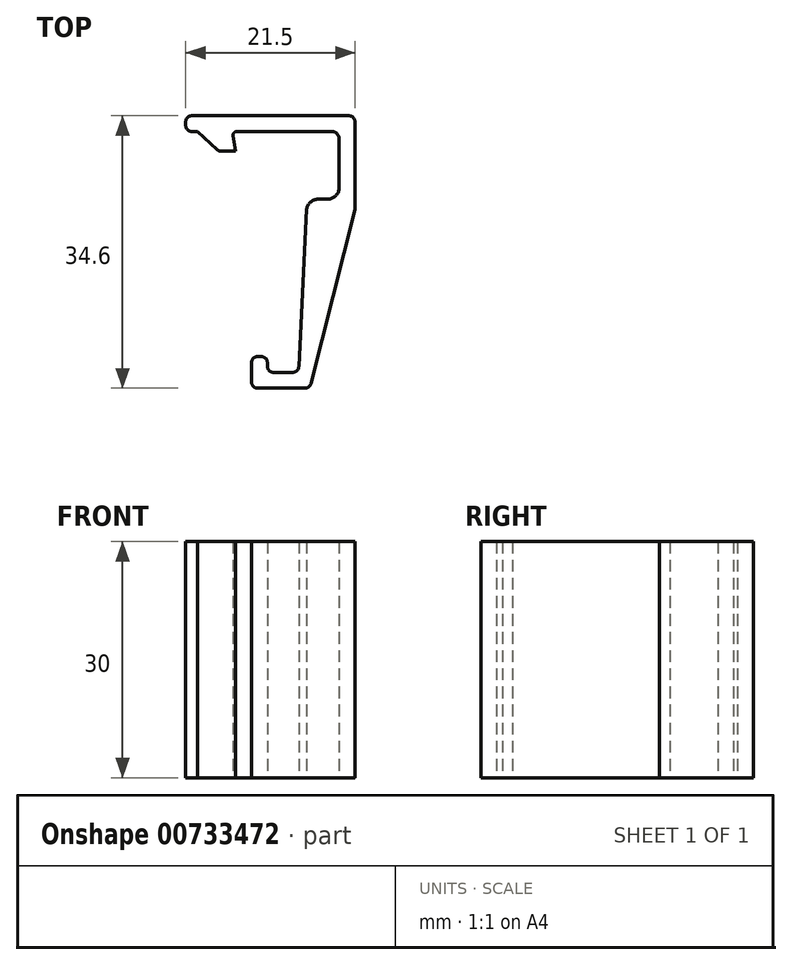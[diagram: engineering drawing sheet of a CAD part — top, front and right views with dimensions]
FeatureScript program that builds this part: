
annotation { "Feature Type Name" : "Feature", "Feature Type Description" : "" }
export const myFeature = defineFeature(function(context is Context, id is Id, definition is map)
    precondition{}
    {
        {
            var Q0;
            Q0=qCreatedBy(makeId("Top.planeOp"),FACE);
            var sketch = newSketch(context, id + "F0", { "sketchPlane" : qUnion([Q0])});
            skLineSegment(sketch, "E0", {"start": v(-1, -0.75) * mm, "end": v(-1, -7.25) * mm});
            skLineSegment(sketch, "E1", {"start": v(12.13, 14.84) * mm, "end": v(12.13, 25.85) * mm});
            skLineSegment(sketch, "E2", {"start": v(11.38, 26.6) * mm, "end": v(-8.62, 26.6) * mm});
            skLineSegment(sketch, "E3", {"start": v(-9.37, 25.85) * mm, "end": v(-9.37, 25.35) * mm});
            skLineSegment(sketch, "E4", {"start": v(-8.62, 24.6) * mm, "end": v(-7.87, 24.6) * mm});
            skLineSegment(sketch, "E5", {"start": v(-4.87, 22.1) * mm, "end": v(-3.37, 22.1) * mm});
            skLineSegment(sketch, "E6", {"start": v(-2.87, 24.6) * mm, "end": v(9.13, 24.6) * mm});
            skLineSegment(sketch, "E7", {"start": v(10.13, 23.6) * mm, "end": v(10.13, 17.5) * mm});
            skLineSegment(sketch, "E8", {"start": v(8.63, 16) * mm, "end": v(7.48, 16) * mm});
            skLineSegment(sketch, "E9", {"start": v(4.25, -6) * mm, "end": v(1.75, -6) * mm});
            skLineSegment(sketch, "E10", {"start": v(1, -5.25) * mm, "end": v(1, -4.75) * mm});
            skLineSegment(sketch, "E11", {"start": v(0.25, -4) * mm, "end": v(-0.25, -4) * mm});
            skArc(sketch, "E12.filletArc", {"start": v(-8.62, 26.6) * mm, "mid": v(-9.15, 26.38) * mm, "end": v(-9.37, 25.85) * mm});
            skArc(sketch, "E13.filletArc", {"start": v(-9.37, 25.35) * mm, "mid": v(-9.15, 24.82) * mm, "end": v(-8.62, 24.6) * mm});
            skPoint(sketch, "E14.visualSharp", {"position": v(-3.37, 22.1) * mm});
            skLineSegment(sketch, "E14.filletArc", {"start": v(-3.37, 22.1) * mm, "end": v(-3.37, 22.1) * mm});
            skPoint(sketch, "E15.visualSharp", {"position": v(-3.37, 24.6) * mm});
            skArc(sketch, "E15.filletArc", {"start": v(-2.87, 24.6) * mm, "mid": v(-3.22, 24.45) * mm, "end": v(-3.37, 24.1) * mm});
            skPoint(sketch, "E16.visualSharp", {"position": v(-6.37, 24.6) * mm});
            skArc(sketch, "E17.filletArc", {"start": v(10.13, 23.6) * mm, "mid": v(9.84, 24.3) * mm, "end": v(9.13, 24.6) * mm});
            skPoint(sketch, "E18.visualSharp", {"position": v(10.13, 16) * mm});
            skArc(sketch, "E18.filletArc", {"start": v(8.63, 16) * mm, "mid": v(9.7, 16.44) * mm, "end": v(10.13, 17.5) * mm});
            skPoint(sketch, "E19.visualSharp", {"position": v(7.13, 16) * mm});
            skArc(sketch, "E19.filletArc", {"start": v(7.48, 16) * mm, "mid": v(6.51, 15.65) * mm, "end": v(6, 14.76) * mm});
            skArc(sketch, "E20.filletArc", {"start": v(12.13, 25.85) * mm, "mid": v(11.91, 26.38) * mm, "end": v(11.38, 26.6) * mm});
            skPoint(sketch, "E21.visualSharp", {"position": v(6, -6) * mm});
            skArc(sketch, "E21.filletArc", {"start": v(4.25, -6) * mm, "mid": v(4.78, -5.78) * mm, "end": v(5, -5.25) * mm});
            skPoint(sketch, "E22.visualSharp", {"position": v(2, -6) * mm});
            skArc(sketch, "E22.filletArc", {"start": v(1, -5.25) * mm, "mid": v(1.22, -5.78) * mm, "end": v(1.75, -6) * mm});
            skPoint(sketch, "E23.visualSharp", {"position": v(2, 0) * mm});
            skArc(sketch, "E23.filletArc", {"start": v(1, -4.75) * mm, "mid": v(0.78, -4.22) * mm, "end": v(0.25, -4) * mm});
            skPoint(sketch, "E24.visualSharp", {"position": v(0, 0) * mm});
            skArc(sketch, "E24.filletArc", {"start": v(-0.25, -4) * mm, "mid": v(-0.78, -4.22) * mm, "end": v(-1, -4.75) * mm});
            skPoint(sketch, "E25.visualSharp", {"position": v(0, -8) * mm});
            skArc(sketch, "E25.filletArc", {"start": v(-1, -7.25) * mm, "mid": v(-0.78, -7.78) * mm, "end": v(-0.25, -8) * mm});
            skPoint(sketch, "E26.visualSharp", {"position": v(8, -8) * mm});
            skLineSegment(sketch, "E27", {"start": v(12.12, 14.67) * mm, "end": v(6.53, -7.43) * mm});
            skPoint(sketch, "E28.visualSharp", {"position": v(12.13, 14.76) * mm});
            skArc(sketch, "E28.filletArc", {"start": v(12.12, 14.67) * mm, "mid": v(12.13, 14.76) * mm, "end": v(12.13, 14.84) * mm});
            skLineSegment(sketch, "E29.trimOffspring", {"start": v(-0.25, -8) * mm, "end": v(5.8, -8) * mm});
            skLineSegment(sketch, "E30", {"start": v(6, 14.76) * mm, "end": v(5, -5.25) * mm});
            skPoint(sketch, "E31.visualSharp", {"position": v(6.4, -8) * mm});
            skArc(sketch, "E31.filletArc", {"start": v(5.8, -8) * mm, "mid": v(6.27, -7.84) * mm, "end": v(6.53, -7.43) * mm});
            skLineSegment(sketch, "E32", {"start": v(-3.37, 22.1) * mm, "end": v(-3.07, 22.1) * mm});
            skLineSegment(sketch, "E33", {"start": v(-3.37, 24.1) * mm, "end": v(-3.07, 22.1) * mm});
            skLineSegment(sketch, "E34", {"start": v(-7.87, 24.6) * mm, "end": v(-5.38, 22.3) * mm});
            skPoint(sketch, "E35.visualSharp", {"position": v(-5.17, 22.1) * mm});
            skArc(sketch, "E35.filletArc", {"start": v(-5.38, 22.3) * mm, "mid": v(-5.15, 22.15) * mm, "end": v(-4.87, 22.1) * mm});
            skSolve(sketch);
        }
        {
            var Q0;
            Q0 = qSketchRegion(id + "F0", true);
            extrude(context, id + "F1", {"entities" : qUnion([Q0]), "depth" : 30 * mm, "offsetDistance" : 25 * mm, "symmetric" : true});
        }
    });
